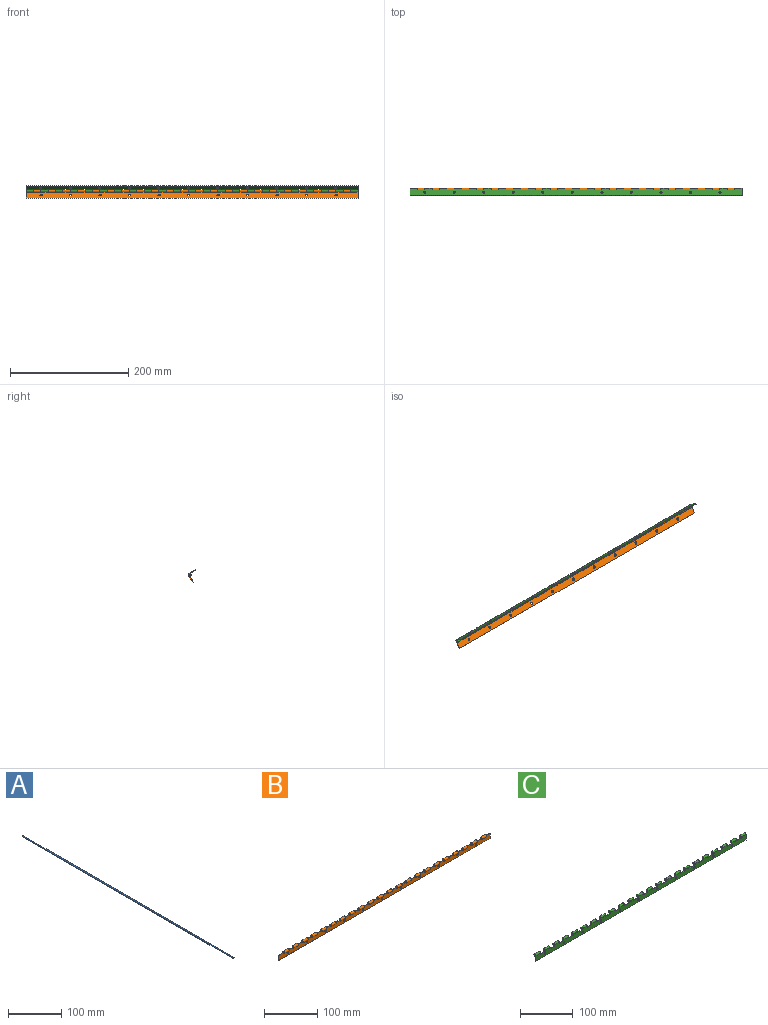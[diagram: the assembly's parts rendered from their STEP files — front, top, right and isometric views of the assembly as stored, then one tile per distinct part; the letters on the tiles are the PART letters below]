
ASSEMBLY  parts=3 mates=1
PART A: 3 faces, bbox 2.8x562.5x2.8 mm
  f0: cylinder r=1.4mm len=562.5mm, axis (0,1,0), area 4948mm2, adj f1,f2
  f1: plane 2.8x2.8mm, normal (0,-1,0), area 6.2mm2, adj f0
  f2: plane 2.8x2.8mm, normal (0,1,0), area 6.2mm2, adj f0
PART B: 193 faces, bbox 562.5x5x16 mm
  f0: plane 562.5x13.5mm, normal (0,-1,0), area 6880.5mm2, adj f4,f5,f8,f11,f14,f17,f20,f23
  f1: plane 562.5x13.5mm, normal (0,1,0), area 6880.5mm2, adj f3,f5,f7,f10,f13,f16,f19,f22
  f2: plane 12.5x0.87mm, normal (0,0.87,0.5), area 12.5mm2, adj f3,f4,f179,f182
  f3: cylinder r=2.5mm len=12.5mm, axis (-1,0,0), area 163.6mm2, adj f1,f2,f179,f182
  f4: cylinder r=1.5mm len=12.5mm, axis (-1,0,0), area 98.2mm2, adj f0,f2,f179,f182
  f5: plane 11.5x1mm, normal (1,0,0), area 11.5mm2, adj f0,f1,f70,f181
  f6: plane 12.5x0.87mm, normal (0,0.87,0.5), area 12.5mm2, adj f7,f8,f174,f178
  f7: cylinder r=2.5mm len=12.5mm, axis (-1,0,0), area 163.6mm2, adj f1,f6,f174,f178
  f8: cylinder r=1.5mm len=12.5mm, axis (-1,0,0), area 98.2mm2, adj f0,f6,f174,f178
  f9: plane 12.5x0.87mm, normal (0,0.87,0.5), area 12.5mm2, adj f10,f11,f169,f173
  f10: cylinder r=2.5mm len=12.5mm, axis (-1,0,0), area 163.6mm2, adj f1,f9,f169,f173
  f11: cylinder r=1.5mm len=12.5mm, axis (-1,0,0), area 98.2mm2, adj f0,f9,f169,f173
  f12: plane 12.5x0.87mm, normal (0,0.87,0.5), area 12.5mm2, adj f13,f14,f164,f168
  f13: cylinder r=2.5mm len=12.5mm, axis (-1,0,0), area 163.6mm2, adj f1,f12,f164,f168
  f14: cylinder r=1.5mm len=12.5mm, axis (-1,0,0), area 98.2mm2, adj f0,f12,f164,f168
  f15: plane 12.5x0.87mm, normal (0,0.87,0.5), area 12.5mm2, adj f16,f17,f159,f163
  f16: cylinder r=2.5mm len=12.5mm, axis (-1,0,0), area 163.6mm2, adj f1,f15,f159,f163
  f17: cylinder r=1.5mm len=12.5mm, axis (-1,0,0), area 98.2mm2, adj f0,f15,f159,f163
  f18: plane 12.5x0.87mm, normal (0,0.87,0.5), area 12.5mm2, adj f19,f20,f154,f158
  f19: cylinder r=2.5mm len=12.5mm, axis (-1,0,0), area 163.6mm2, adj f1,f18,f154,f158
  f20: cylinder r=1.5mm len=12.5mm, axis (-1,0,0), area 98.2mm2, adj f0,f18,f154,f158
  f21: plane 12.5x0.87mm, normal (0,0.87,0.5), area 12.5mm2, adj f22,f23,f149,f153
  f22: cylinder r=2.5mm len=12.5mm, axis (-1,0,0), area 163.6mm2, adj f1,f21,f149,f153
  f23: cylinder r=1.5mm len=12.5mm, axis (-1,0,0), area 98.2mm2, adj f0,f21,f149,f153
  f24: plane 12.5x0.87mm, normal (0,0.87,0.5), area 12.5mm2, adj f25,f26,f144,f148
  f25: cylinder r=2.5mm len=12.5mm, axis (-1,0,0), area 163.6mm2, adj f1,f24,f144,f148
  f26: cylinder r=1.5mm len=12.5mm, axis (-1,0,0), area 98.2mm2, adj f0,f24,f144,f148
  f27: plane 12.5x0.87mm, normal (0,0.87,0.5), area 12.5mm2, adj f28,f29,f139,f143
  f28: cylinder r=2.5mm len=12.5mm, axis (-1,0,0), area 163.6mm2, adj f1,f27,f139,f143
  f29: cylinder r=1.5mm len=12.5mm, axis (-1,0,0), area 98.2mm2, adj f0,f27,f139,f143
  f30: plane 12.5x0.87mm, normal (0,0.87,0.5), area 12.5mm2, adj f31,f32,f134,f138
  f31: cylinder r=2.5mm len=12.5mm, axis (-1,0,0), area 163.6mm2, adj f1,f30,f134,f138
  f32: cylinder r=1.5mm len=12.5mm, axis (-1,0,0), area 98.2mm2, adj f0,f30,f134,f138
  f33: plane 12.5x0.87mm, normal (0,0.87,0.5), area 12.5mm2, adj f34,f35,f129,f133
  f34: cylinder r=2.5mm len=12.5mm, axis (-1,0,0), area 163.6mm2, adj f1,f33,f129,f133
  f35: cylinder r=1.5mm len=12.5mm, axis (-1,0,0), area 98.2mm2, adj f0,f33,f129,f133
  f36: plane 12.5x0.87mm, normal (0,0.87,0.5), area 12.5mm2, adj f37,f38,f124,f128
  f37: cylinder r=2.5mm len=12.5mm, axis (-1,0,0), area 163.6mm2, adj f1,f36,f124,f128
  f38: cylinder r=1.5mm len=12.5mm, axis (-1,0,0), area 98.2mm2, adj f0,f36,f124,f128
  f39: plane 12.5x0.87mm, normal (0,0.87,0.5), area 12.5mm2, adj f40,f41,f119,f123
  f40: cylinder r=2.5mm len=12.5mm, axis (-1,0,0), area 163.6mm2, adj f1,f39,f119,f123
  f41: cylinder r=1.5mm len=12.5mm, axis (-1,0,0), area 98.2mm2, adj f0,f39,f119,f123
  f42: plane 12.5x0.87mm, normal (0,0.87,0.5), area 12.5mm2, adj f43,f44,f114,f118
  f43: cylinder r=2.5mm len=12.5mm, axis (-1,0,0), area 163.6mm2, adj f1,f42,f114,f118
  f44: cylinder r=1.5mm len=12.5mm, axis (-1,0,0), area 98.2mm2, adj f0,f42,f114,f118
  f45: plane 12.5x0.87mm, normal (0,0.87,0.5), area 12.5mm2, adj f46,f47,f109,f113
  f46: cylinder r=2.5mm len=12.5mm, axis (-1,0,0), area 163.6mm2, adj f1,f45,f109,f113
  f47: cylinder r=1.5mm len=12.5mm, axis (-1,0,0), area 98.2mm2, adj f0,f45,f109,f113
  f48: plane 12.5x0.87mm, normal (0,0.87,0.5), area 12.5mm2, adj f49,f50,f104,f108
  f49: cylinder r=2.5mm len=12.5mm, axis (-1,0,0), area 163.6mm2, adj f1,f48,f104,f108
  f50: cylinder r=1.5mm len=12.5mm, axis (-1,0,0), area 98.2mm2, adj f0,f48,f104,f108
  f51: plane 12.5x0.87mm, normal (0,0.87,0.5), area 12.5mm2, adj f52,f53,f99,f103
  f52: cylinder r=2.5mm len=12.5mm, axis (-1,0,0), area 163.6mm2, adj f1,f51,f99,f103
  f53: cylinder r=1.5mm len=12.5mm, axis (-1,0,0), area 98.2mm2, adj f0,f51,f99,f103
  f54: plane 12.5x0.87mm, normal (0,0.87,0.5), area 12.5mm2, adj f55,f56,f94,f98
  f55: cylinder r=2.5mm len=12.5mm, axis (-1,0,0), area 163.6mm2, adj f1,f54,f94,f98
  f56: cylinder r=1.5mm len=12.5mm, axis (-1,0,0), area 98.2mm2, adj f0,f54,f94,f98
  f57: plane 12.5x0.87mm, normal (0,0.87,0.5), area 12.5mm2, adj f58,f59,f89,f93
  f58: cylinder r=2.5mm len=12.5mm, axis (-1,0,0), area 163.6mm2, adj f1,f57,f89,f93
  f59: cylinder r=1.5mm len=12.5mm, axis (-1,0,0), area 98.2mm2, adj f0,f57,f89,f93
  f60: plane 12.5x0.87mm, normal (0,0.87,0.5), area 12.5mm2, adj f61,f62,f84,f88
  f61: cylinder r=2.5mm len=12.5mm, axis (-1,0,0), area 163.6mm2, adj f1,f60,f84,f88
  f62: cylinder r=1.5mm len=12.5mm, axis (-1,0,0), area 98.2mm2, adj f0,f60,f84,f88
  f63: plane 12.5x0.87mm, normal (0,0.87,0.5), area 12.5mm2, adj f64,f65,f78,f83
  f64: cylinder r=2.5mm len=12.5mm, axis (-1,0,0), area 163.6mm2, adj f1,f63,f78,f83
  f65: cylinder r=1.5mm len=12.5mm, axis (-1,0,0), area 98.2mm2, adj f0,f63,f78,f83
  f66: plane 12.5x0.87mm, normal (0,0.87,0.5), area 12.5mm2, adj f67,f68,f73,f77
  f67: cylinder r=2.5mm len=12.5mm, axis (-1,0,0), area 163.6mm2, adj f1,f66,f73,f77
  f68: cylinder r=1.5mm len=12.5mm, axis (-1,0,0), area 98.2mm2, adj f0,f66,f73,f77
  f69: plane 11.5x1mm, normal (-1,0,0), area 11.5mm2, adj f0,f1,f70,f71
  f70: plane 562.5x1mm, normal (0,0,-1), area 562.5mm2, adj f0,f1,f5,f69
  f71: plane 12.5x1mm, normal (0,0,1), area 12.5mm2, adj f0,f1,f69,f72
  f72: plane 2x1mm, normal (-1,0,0), area 2mm2, adj f0,f1,f71,f73
  f73: plane 5x5mm, normal (-1,0,0), area 10.5mm2, adj f66,f67,f68,f72
  f74: plane 12.5x1mm, normal (0,0,1), area 12.5mm2, adj f0,f1,f75,f76
  f75: plane 2x1mm, normal (1,0,0), area 2mm2, adj f0,f1,f74,f77
  f76: plane 2x1mm, normal (-1,0,0), area 2mm2, adj f0,f1,f74,f78
  f77: plane 5x5mm, normal (1,0,0), area 10.5mm2, adj f66,f67,f68,f75
  f78: plane 5x5mm, normal (-1,0,0), area 10.5mm2, adj f63,f64,f65,f76
  f79: cylinder r=2mm len=4mm, axis (0,1,0), area 12.6mm2, adj f0,f1
  f80: plane 12.5x1mm, normal (0,0,1), area 12.5mm2, adj f0,f1,f81,f82
  f81: plane 2x1mm, normal (1,0,0), area 2mm2, adj f0,f1,f80,f83
  f82: plane 2x1mm, normal (-1,0,0), area 2mm2, adj f0,f1,f80,f84
  f83: plane 5x5mm, normal (1,0,0), area 10.5mm2, adj f63,f64,f65,f81
  f84: plane 5x5mm, normal (-1,0,0), area 10.5mm2, adj f60,f61,f62,f82
  f85: plane 12.5x1mm, normal (0,0,1), area 12.5mm2, adj f0,f1,f86,f87
  f86: plane 2x1mm, normal (1,0,0), area 2mm2, adj f0,f1,f85,f88
  f87: plane 2x1mm, normal (-1,0,0), area 2mm2, adj f0,f1,f85,f89
  f88: plane 5x5mm, normal (1,0,0), area 10.5mm2, adj f60,f61,f62,f86
  f89: plane 5x5mm, normal (-1,0,0), area 10.5mm2, adj f57,f58,f59,f87
  f90: plane 12.5x1mm, normal (0,0,1), area 12.5mm2, adj f0,f1,f91,f92
  f91: plane 2x1mm, normal (1,0,0), area 2mm2, adj f0,f1,f90,f93
  f92: plane 2x1mm, normal (-1,0,0), area 2mm2, adj f0,f1,f90,f94
  f93: plane 5x5mm, normal (1,0,0), area 10.5mm2, adj f57,f58,f59,f91
  f94: plane 5x5mm, normal (-1,0,0), area 10.5mm2, adj f54,f55,f56,f92
  f95: plane 12.5x1mm, normal (0,0,1), area 12.5mm2, adj f0,f1,f96,f97
  f96: plane 2x1mm, normal (1,0,0), area 2mm2, adj f0,f1,f95,f98
  f97: plane 2x1mm, normal (-1,0,0), area 2mm2, adj f0,f1,f95,f99
  f98: plane 5x5mm, normal (1,0,0), area 10.5mm2, adj f54,f55,f56,f96
  f99: plane 5x5mm, normal (-1,0,0), area 10.5mm2, adj f51,f52,f53,f97
  f100: plane 12.5x1mm, normal (0,0,1), area 12.5mm2, adj f0,f1,f101,f102
  f101: plane 2x1mm, normal (1,0,0), area 2mm2, adj f0,f1,f100,f103
  f102: plane 2x1mm, normal (-1,0,0), area 2mm2, adj f0,f1,f100,f104
  f103: plane 5x5mm, normal (1,0,0), area 10.5mm2, adj f51,f52,f53,f101
  f104: plane 5x5mm, normal (-1,0,0), area 10.5mm2, adj f48,f49,f50,f102
  f105: plane 12.5x1mm, normal (0,0,1), area 12.5mm2, adj f0,f1,f106,f107
  f106: plane 2x1mm, normal (1,0,0), area 2mm2, adj f0,f1,f105,f108
  f107: plane 2x1mm, normal (-1,0,0), area 2mm2, adj f0,f1,f105,f109
  f108: plane 5x5mm, normal (1,0,0), area 10.5mm2, adj f48,f49,f50,f106
  f109: plane 5x5mm, normal (-1,0,0), area 10.5mm2, adj f45,f46,f47,f107
  f110: plane 12.5x1mm, normal (0,0,1), area 12.5mm2, adj f0,f1,f111,f112
  f111: plane 2x1mm, normal (1,0,0), area 2mm2, adj f0,f1,f110,f113
  f112: plane 2x1mm, normal (-1,0,0), area 2mm2, adj f0,f1,f110,f114
  f113: plane 5x5mm, normal (1,0,0), area 10.5mm2, adj f45,f46,f47,f111
  f114: plane 5x5mm, normal (-1,0,0), area 10.5mm2, adj f42,f43,f44,f112
  f115: plane 12.5x1mm, normal (0,0,1), area 12.5mm2, adj f0,f1,f116,f117
  f116: plane 2x1mm, normal (1,0,0), area 2mm2, adj f0,f1,f115,f118
  f117: plane 2x1mm, normal (-1,0,0), area 2mm2, adj f0,f1,f115,f119
  f118: plane 5x5mm, normal (1,0,0), area 10.5mm2, adj f42,f43,f44,f116
  f119: plane 5x5mm, normal (-1,0,0), area 10.5mm2, adj f39,f40,f41,f117
  f120: plane 12.5x1mm, normal (0,0,1), area 12.5mm2, adj f0,f1,f121,f122
  f121: plane 2x1mm, normal (1,0,0), area 2mm2, adj f0,f1,f120,f123
  f122: plane 2x1mm, normal (-1,0,0), area 2mm2, adj f0,f1,f120,f124
  f123: plane 5x5mm, normal (1,0,0), area 10.5mm2, adj f39,f40,f41,f121
  f124: plane 5x5mm, normal (-1,0,0), area 10.5mm2, adj f36,f37,f38,f122
  f125: plane 12.5x1mm, normal (0,0,1), area 12.5mm2, adj f0,f1,f126,f127
  f126: plane 2x1mm, normal (1,0,0), area 2mm2, adj f0,f1,f125,f128
  f127: plane 2x1mm, normal (-1,0,0), area 2mm2, adj f0,f1,f125,f129
  f128: plane 5x5mm, normal (1,0,0), area 10.5mm2, adj f36,f37,f38,f126
  f129: plane 5x5mm, normal (-1,0,0), area 10.5mm2, adj f33,f34,f35,f127
  f130: plane 12.5x1mm, normal (0,0,1), area 12.5mm2, adj f0,f1,f131,f132
  f131: plane 2x1mm, normal (1,0,0), area 2mm2, adj f0,f1,f130,f133
  f132: plane 2x1mm, normal (-1,0,0), area 2mm2, adj f0,f1,f130,f134
  f133: plane 5x5mm, normal (1,0,0), area 10.5mm2, adj f33,f34,f35,f131
  f134: plane 5x5mm, normal (-1,0,0), area 10.5mm2, adj f30,f31,f32,f132
  f135: plane 12.5x1mm, normal (0,0,1), area 12.5mm2, adj f0,f1,f136,f137
  f136: plane 2x1mm, normal (1,0,0), area 2mm2, adj f0,f1,f135,f138
  f137: plane 2x1mm, normal (-1,0,0), area 2mm2, adj f0,f1,f135,f139
  f138: plane 5x5mm, normal (1,0,0), area 10.5mm2, adj f30,f31,f32,f136
  f139: plane 5x5mm, normal (-1,0,0), area 10.5mm2, adj f27,f28,f29,f137
  f140: plane 12.5x1mm, normal (0,0,1), area 12.5mm2, adj f0,f1,f141,f142
  f141: plane 2x1mm, normal (1,0,0), area 2mm2, adj f0,f1,f140,f143
  f142: plane 2x1mm, normal (-1,0,0), area 2mm2, adj f0,f1,f140,f144
  f143: plane 5x5mm, normal (1,0,0), area 10.5mm2, adj f27,f28,f29,f141
  f144: plane 5x5mm, normal (-1,0,0), area 10.5mm2, adj f24,f25,f26,f142
  f145: plane 12.5x1mm, normal (0,0,1), area 12.5mm2, adj f0,f1,f146,f147
  f146: plane 2x1mm, normal (1,0,0), area 2mm2, adj f0,f1,f145,f148
  f147: plane 2x1mm, normal (-1,0,0), area 2mm2, adj f0,f1,f145,f149
  f148: plane 5x5mm, normal (1,0,0), area 10.5mm2, adj f24,f25,f26,f146
  f149: plane 5x5mm, normal (-1,0,0), area 10.5mm2, adj f21,f22,f23,f147
  f150: plane 12.5x1mm, normal (0,0,1), area 12.5mm2, adj f0,f1,f151,f152
  f151: plane 2x1mm, normal (1,0,0), area 2mm2, adj f0,f1,f150,f153
  f152: plane 2x1mm, normal (-1,0,0), area 2mm2, adj f0,f1,f150,f154
  f153: plane 5x5mm, normal (1,0,0), area 10.5mm2, adj f21,f22,f23,f151
  f154: plane 5x5mm, normal (-1,0,0), area 10.5mm2, adj f18,f19,f20,f152
  f155: plane 12.5x1mm, normal (0,0,1), area 12.5mm2, adj f0,f1,f156,f157
  f156: plane 2x1mm, normal (1,0,0), area 2mm2, adj f0,f1,f155,f158
  f157: plane 2x1mm, normal (-1,0,0), area 2mm2, adj f0,f1,f155,f159
  f158: plane 5x5mm, normal (1,0,0), area 10.5mm2, adj f18,f19,f20,f156
  f159: plane 5x5mm, normal (-1,0,0), area 10.5mm2, adj f15,f16,f17,f157
  f160: plane 12.5x1mm, normal (0,0,1), area 12.5mm2, adj f0,f1,f161,f162
  f161: plane 2x1mm, normal (1,0,0), area 2mm2, adj f0,f1,f160,f163
  f162: plane 2x1mm, normal (-1,0,0), area 2mm2, adj f0,f1,f160,f164
  f163: plane 5x5mm, normal (1,0,0), area 10.5mm2, adj f15,f16,f17,f161
  f164: plane 5x5mm, normal (-1,0,0), area 10.5mm2, adj f12,f13,f14,f162
  f165: plane 12.5x1mm, normal (0,0,1), area 12.5mm2, adj f0,f1,f166,f167
  f166: plane 2x1mm, normal (1,0,0), area 2mm2, adj f0,f1,f165,f168
  f167: plane 2x1mm, normal (-1,0,0), area 2mm2, adj f0,f1,f165,f169
  f168: plane 5x5mm, normal (1,0,0), area 10.5mm2, adj f12,f13,f14,f166
  f169: plane 5x5mm, normal (-1,0,0), area 10.5mm2, adj f9,f10,f11,f167
  f170: plane 12.5x1mm, normal (0,0,1), area 12.5mm2, adj f0,f1,f171,f172
  f171: plane 2x1mm, normal (1,0,0), area 2mm2, adj f0,f1,f170,f173
  f172: plane 2x1mm, normal (-1,0,0), area 2mm2, adj f0,f1,f170,f174
  f173: plane 5x5mm, normal (1,0,0), area 10.5mm2, adj f9,f10,f11,f171
  f174: plane 5x5mm, normal (-1,0,0), area 10.5mm2, adj f6,f7,f8,f172
  f175: plane 12.5x1mm, normal (0,0,1), area 12.5mm2, adj f0,f1,f176,f177
  f176: plane 2x1mm, normal (1,0,0), area 2mm2, adj f0,f1,f175,f178
  f177: plane 2x1mm, normal (-1,0,0), area 2mm2, adj f0,f1,f175,f179
  f178: plane 5x5mm, normal (1,0,0), area 10.5mm2, adj f6,f7,f8,f176
  f179: plane 5x5mm, normal (-1,0,0), area 10.5mm2, adj f2,f3,f4,f177
  f180: plane 2x1mm, normal (1,0,0), area 2mm2, adj f0,f1,f181,f182
  f181: plane 12.5x1mm, normal (0,0,1), area 12.5mm2, adj f0,f1,f5,f180
  f182: plane 5x5mm, normal (1,0,0), area 10.5mm2, adj f2,f3,f4,f180
  f183: cylinder r=2mm len=4mm, axis (0,1,0), area 12.6mm2, adj f0,f1
  f184: cylinder r=2mm len=4mm, axis (0,1,0), area 12.6mm2, adj f0,f1
  f185: cylinder r=2mm len=4mm, axis (0,1,0), area 12.6mm2, adj f0,f1
  f186: cylinder r=2mm len=4mm, axis (0,1,0), area 12.6mm2, adj f0,f1
  f187: cylinder r=2mm len=4mm, axis (0,1,0), area 12.6mm2, adj f0,f1
  f188: cylinder r=2mm len=4mm, axis (0,1,0), area 12.6mm2, adj f0,f1
  f189: cylinder r=2mm len=4mm, axis (0,1,0), area 12.6mm2, adj f0,f1
  f190: cylinder r=2mm len=4mm, axis (0,1,0), area 12.6mm2, adj f0,f1
  f191: cylinder r=2mm len=4mm, axis (0,1,0), area 12.6mm2, adj f0,f1
  f192: cylinder r=2mm len=4mm, axis (0,1,0), area 12.6mm2, adj f0,f1
PART C: 153 faces, bbox 562.5x5x15.5 mm
  f0: plane 12.5x0.87mm, normal (0,-0.87,0.5), area 12.5mm2, adj f1,f2,f137,f139
  f1: cylinder r=2.5mm len=12.5mm, axis (1,0,0), area 163.6mm2, adj f0,f69,f137,f139
  f2: cylinder r=1.5mm len=12.5mm, axis (1,0,0), area 98.2mm2, adj f0,f70,f137,f139
  f3: plane 12.5x0.87mm, normal (0,-0.87,0.5), area 12.5mm2, adj f4,f5,f134,f136
  f4: cylinder r=2.5mm len=12.5mm, axis (1,0,0), area 163.6mm2, adj f3,f69,f134,f136
  f5: cylinder r=1.5mm len=12.5mm, axis (1,0,0), area 98.2mm2, adj f3,f70,f134,f136
  f6: plane 12.5x0.87mm, normal (0,-0.87,0.5), area 12.5mm2, adj f7,f8,f131,f133
  f7: cylinder r=2.5mm len=12.5mm, axis (1,0,0), area 163.6mm2, adj f6,f69,f131,f133
  f8: cylinder r=1.5mm len=12.5mm, axis (1,0,0), area 98.2mm2, adj f6,f70,f131,f133
  f9: plane 12.5x0.87mm, normal (0,-0.87,0.5), area 12.5mm2, adj f10,f11,f128,f130
  f10: cylinder r=2.5mm len=12.5mm, axis (1,0,0), area 163.6mm2, adj f9,f69,f128,f130
  f11: cylinder r=1.5mm len=12.5mm, axis (1,0,0), area 98.2mm2, adj f9,f70,f128,f130
  f12: plane 12.5x0.87mm, normal (0,-0.87,0.5), area 12.5mm2, adj f13,f14,f125,f127
  f13: cylinder r=2.5mm len=12.5mm, axis (1,0,0), area 163.6mm2, adj f12,f69,f125,f127
  f14: cylinder r=1.5mm len=12.5mm, axis (1,0,0), area 98.2mm2, adj f12,f70,f125,f127
  f15: plane 12.5x0.87mm, normal (0,-0.87,0.5), area 12.5mm2, adj f16,f17,f122,f124
  f16: cylinder r=2.5mm len=12.5mm, axis (1,0,0), area 163.6mm2, adj f15,f69,f122,f124
  f17: cylinder r=1.5mm len=12.5mm, axis (1,0,0), area 98.2mm2, adj f15,f70,f122,f124
  f18: plane 12.5x0.87mm, normal (0,-0.87,0.5), area 12.5mm2, adj f19,f20,f119,f121
  f19: cylinder r=2.5mm len=12.5mm, axis (1,0,0), area 163.6mm2, adj f18,f69,f119,f121
  f20: cylinder r=1.5mm len=12.5mm, axis (1,0,0), area 98.2mm2, adj f18,f70,f119,f121
  f21: plane 12.5x0.87mm, normal (0,-0.87,0.5), area 12.5mm2, adj f22,f23,f116,f118
  f22: cylinder r=2.5mm len=12.5mm, axis (1,0,0), area 163.6mm2, adj f21,f69,f116,f118
  f23: cylinder r=1.5mm len=12.5mm, axis (1,0,0), area 98.2mm2, adj f21,f70,f116,f118
  f24: plane 12.5x0.87mm, normal (0,-0.87,0.5), area 12.5mm2, adj f25,f26,f113,f115
  f25: cylinder r=2.5mm len=12.5mm, axis (1,0,0), area 163.6mm2, adj f24,f69,f113,f115
  f26: cylinder r=1.5mm len=12.5mm, axis (1,0,0), area 98.2mm2, adj f24,f70,f113,f115
  f27: plane 12.5x0.87mm, normal (0,-0.87,0.5), area 12.5mm2, adj f28,f29,f110,f112
  f28: cylinder r=2.5mm len=12.5mm, axis (1,0,0), area 163.6mm2, adj f27,f69,f110,f112
  f29: cylinder r=1.5mm len=12.5mm, axis (1,0,0), area 98.2mm2, adj f27,f70,f110,f112
  f30: plane 12.5x0.87mm, normal (0,-0.87,0.5), area 12.5mm2, adj f31,f32,f107,f109
  f31: cylinder r=2.5mm len=12.5mm, axis (1,0,0), area 163.6mm2, adj f30,f69,f107,f109
  f32: cylinder r=1.5mm len=12.5mm, axis (1,0,0), area 98.2mm2, adj f30,f70,f107,f109
  f33: plane 12.5x0.87mm, normal (0,-0.87,0.5), area 12.5mm2, adj f34,f35,f104,f106
  f34: cylinder r=2.5mm len=12.5mm, axis (1,0,0), area 163.6mm2, adj f33,f69,f104,f106
  f35: cylinder r=1.5mm len=12.5mm, axis (1,0,0), area 98.2mm2, adj f33,f70,f104,f106
  f36: plane 12.5x0.87mm, normal (0,-0.87,0.5), area 12.5mm2, adj f37,f38,f101,f103
  f37: cylinder r=2.5mm len=12.5mm, axis (1,0,0), area 163.6mm2, adj f36,f69,f101,f103
  f38: cylinder r=1.5mm len=12.5mm, axis (1,0,0), area 98.2mm2, adj f36,f70,f101,f103
  f39: plane 12.5x0.87mm, normal (0,-0.87,0.5), area 12.5mm2, adj f40,f41,f98,f100
  f40: cylinder r=2.5mm len=12.5mm, axis (1,0,0), area 163.6mm2, adj f39,f69,f98,f100
  f41: cylinder r=1.5mm len=12.5mm, axis (1,0,0), area 98.2mm2, adj f39,f70,f98,f100
  f42: plane 12.5x0.87mm, normal (0,-0.87,0.5), area 12.5mm2, adj f43,f44,f95,f97
  f43: cylinder r=2.5mm len=12.5mm, axis (1,0,0), area 163.6mm2, adj f42,f69,f95,f97
  f44: cylinder r=1.5mm len=12.5mm, axis (1,0,0), area 98.2mm2, adj f42,f70,f95,f97
  f45: plane 12.5x0.87mm, normal (0,-0.87,0.5), area 12.5mm2, adj f46,f47,f92,f94
  f46: cylinder r=2.5mm len=12.5mm, axis (1,0,0), area 163.6mm2, adj f45,f69,f92,f94
  f47: cylinder r=1.5mm len=12.5mm, axis (1,0,0), area 98.2mm2, adj f45,f70,f92,f94
  f48: plane 12.5x0.87mm, normal (0,-0.87,0.5), area 12.5mm2, adj f49,f50,f89,f91
  f49: cylinder r=2.5mm len=12.5mm, axis (1,0,0), area 163.6mm2, adj f48,f69,f89,f91
  f50: cylinder r=1.5mm len=12.5mm, axis (1,0,0), area 98.2mm2, adj f48,f70,f89,f91
  f51: plane 12.5x0.87mm, normal (0,-0.87,0.5), area 12.5mm2, adj f52,f53,f86,f88
  f52: cylinder r=2.5mm len=12.5mm, axis (1,0,0), area 163.6mm2, adj f51,f69,f86,f88
  f53: cylinder r=1.5mm len=12.5mm, axis (1,0,0), area 98.2mm2, adj f51,f70,f86,f88
  f54: plane 12.5x0.87mm, normal (0,-0.87,0.5), area 12.5mm2, adj f55,f56,f83,f85
  f55: cylinder r=2.5mm len=12.5mm, axis (1,0,0), area 163.6mm2, adj f54,f69,f83,f85
  f56: cylinder r=1.5mm len=12.5mm, axis (1,0,0), area 98.2mm2, adj f54,f70,f83,f85
  f57: plane 12.5x0.87mm, normal (0,-0.87,0.5), area 12.5mm2, adj f58,f59,f80,f82
  f58: cylinder r=2.5mm len=12.5mm, axis (1,0,0), area 163.6mm2, adj f57,f69,f80,f82
  f59: cylinder r=1.5mm len=12.5mm, axis (1,0,0), area 98.2mm2, adj f57,f70,f80,f82
  f60: plane 12.5x0.87mm, normal (0,-0.87,0.5), area 12.5mm2, adj f61,f62,f77,f79
  f61: cylinder r=2.5mm len=12.5mm, axis (1,0,0), area 163.6mm2, adj f60,f69,f77,f79
  f62: cylinder r=1.5mm len=12.5mm, axis (1,0,0), area 98.2mm2, adj f60,f70,f77,f79
  f63: plane 12.5x0.87mm, normal (0,-0.87,0.5), area 12.5mm2, adj f64,f65,f72,f76
  f64: cylinder r=2.5mm len=12.5mm, axis (1,0,0), area 163.6mm2, adj f63,f69,f72,f76
  f65: cylinder r=1.5mm len=12.5mm, axis (1,0,0), area 98.2mm2, adj f63,f70,f72,f76
  f66: plane 13x1mm, normal (-1,0,0), area 13mm2, adj f67,f69,f70,f72
  f67: plane 562.5x1mm, normal (0,0,-1), area 562.5mm2, adj f66,f68,f69,f70
  f68: plane 13x1mm, normal (1,0,0), area 13mm2, adj f67,f69,f70,f73
  f69: plane 562.5x13mm, normal (0,-1,0), area 6486.8mm2, adj f1,f4,f7,f10,f13,f16,f19,f22
  f70: plane 562.5x13mm, normal (0,1,0), area 6486.8mm2, adj f2,f5,f8,f11,f14,f17,f20,f23
  f71: plane 12.5x0.87mm, normal (0,-0.87,0.5), area 12.5mm2, adj f73,f74,f75,f140
  f72: plane 5x5mm, normal (-1,0,0), area 10.5mm2, adj f63,f64,f65,f66
  f73: plane 5x5mm, normal (1,0,0), area 10.5mm2, adj f68,f71,f74,f75
  f74: cylinder r=2.5mm len=12.5mm, axis (1,0,0), area 163.6mm2, adj f69,f71,f73,f140
  f75: cylinder r=1.5mm len=12.5mm, axis (1,0,0), area 98.2mm2, adj f70,f71,f73,f140
  f76: plane 5x5mm, normal (1,0,0), area 13mm2, adj f63,f64,f65,f69,f70,f78
  f77: plane 5x5mm, normal (-1,0,0), area 13mm2, adj f60,f61,f62,f69,f70,f78
  f78: plane 12.5x1mm, normal (0,0,1), area 12.5mm2, adj f69,f70,f76,f77
  f79: plane 5x5mm, normal (1,0,0), area 13mm2, adj f60,f61,f62,f69,f70,f81
  f80: plane 5x5mm, normal (-1,0,0), area 13mm2, adj f57,f58,f59,f69,f70,f81
  f81: plane 12.5x1mm, normal (0,0,1), area 12.5mm2, adj f69,f70,f79,f80
  f82: plane 5x5mm, normal (1,0,0), area 13mm2, adj f57,f58,f59,f69,f70,f84
  f83: plane 5x5mm, normal (-1,0,0), area 13mm2, adj f54,f55,f56,f69,f70,f84
  f84: plane 12.5x1mm, normal (0,0,1), area 12.5mm2, adj f69,f70,f82,f83
  f85: plane 5x5mm, normal (1,0,0), area 13mm2, adj f54,f55,f56,f69,f70,f87
  f86: plane 5x5mm, normal (-1,0,0), area 13mm2, adj f51,f52,f53,f69,f70,f87
  f87: plane 12.5x1mm, normal (0,0,1), area 12.5mm2, adj f69,f70,f85,f86
  f88: plane 5x5mm, normal (1,0,0), area 13mm2, adj f51,f52,f53,f69,f70,f90
  f89: plane 5x5mm, normal (-1,0,0), area 13mm2, adj f48,f49,f50,f69,f70,f90
  f90: plane 12.5x1mm, normal (0,0,1), area 12.5mm2, adj f69,f70,f88,f89
  f91: plane 5x5mm, normal (1,0,0), area 13mm2, adj f48,f49,f50,f69,f70,f93
  f92: plane 5x5mm, normal (-1,0,0), area 13mm2, adj f45,f46,f47,f69,f70,f93
  f93: plane 12.5x1mm, normal (0,0,1), area 12.5mm2, adj f69,f70,f91,f92
  f94: plane 5x5mm, normal (1,0,0), area 13mm2, adj f45,f46,f47,f69,f70,f96
  f95: plane 5x5mm, normal (-1,0,0), area 13mm2, adj f42,f43,f44,f69,f70,f96
  f96: plane 12.5x1mm, normal (0,0,1), area 12.5mm2, adj f69,f70,f94,f95
  f97: plane 5x5mm, normal (1,0,0), area 13mm2, adj f42,f43,f44,f69,f70,f99
  f98: plane 5x5mm, normal (-1,0,0), area 13mm2, adj f39,f40,f41,f69,f70,f99
  f99: plane 12.5x1mm, normal (0,0,1), area 12.5mm2, adj f69,f70,f97,f98
  f100: plane 5x5mm, normal (1,0,0), area 13mm2, adj f39,f40,f41,f69,f70,f102
  f101: plane 5x5mm, normal (-1,0,0), area 13mm2, adj f36,f37,f38,f69,f70,f102
  f102: plane 12.5x1mm, normal (0,0,1), area 12.5mm2, adj f69,f70,f100,f101
  f103: plane 5x5mm, normal (1,0,0), area 13mm2, adj f36,f37,f38,f69,f70,f105
  f104: plane 5x5mm, normal (-1,0,0), area 13mm2, adj f33,f34,f35,f69,f70,f105
  f105: plane 12.5x1mm, normal (0,0,1), area 12.5mm2, adj f69,f70,f103,f104
  f106: plane 5x5mm, normal (1,0,0), area 13mm2, adj f33,f34,f35,f69,f70,f108
  f107: plane 5x5mm, normal (-1,0,0), area 13mm2, adj f30,f31,f32,f69,f70,f108
  f108: plane 12.5x1mm, normal (0,0,1), area 12.5mm2, adj f69,f70,f106,f107
  f109: plane 5x5mm, normal (1,0,0), area 13mm2, adj f30,f31,f32,f69,f70,f111
  f110: plane 5x5mm, normal (-1,0,0), area 13mm2, adj f27,f28,f29,f69,f70,f111
  f111: plane 12.5x1mm, normal (0,0,1), area 12.5mm2, adj f69,f70,f109,f110
  f112: plane 5x5mm, normal (1,0,0), area 13mm2, adj f27,f28,f29,f69,f70,f114
  f113: plane 5x5mm, normal (-1,0,0), area 13mm2, adj f24,f25,f26,f69,f70,f114
  f114: plane 12.5x1mm, normal (0,0,1), area 12.5mm2, adj f69,f70,f112,f113
  f115: plane 5x5mm, normal (1,0,0), area 13mm2, adj f24,f25,f26,f69,f70,f117
  f116: plane 5x5mm, normal (-1,0,0), area 13mm2, adj f21,f22,f23,f69,f70,f117
  f117: plane 12.5x1mm, normal (0,0,1), area 12.5mm2, adj f69,f70,f115,f116
  f118: plane 5x5mm, normal (1,0,0), area 13mm2, adj f21,f22,f23,f69,f70,f120
  f119: plane 5x5mm, normal (-1,0,0), area 13mm2, adj f18,f19,f20,f69,f70,f120
  f120: plane 12.5x1mm, normal (0,0,1), area 12.5mm2, adj f69,f70,f118,f119
  f121: plane 5x5mm, normal (1,0,0), area 13mm2, adj f18,f19,f20,f69,f70,f123
  f122: plane 5x5mm, normal (-1,0,0), area 13mm2, adj f15,f16,f17,f69,f70,f123
  f123: plane 12.5x1mm, normal (0,0,1), area 12.5mm2, adj f69,f70,f121,f122
  f124: plane 5x5mm, normal (1,0,0), area 13mm2, adj f15,f16,f17,f69,f70,f126
  f125: plane 5x5mm, normal (-1,0,0), area 13mm2, adj f12,f13,f14,f69,f70,f126
  f126: plane 12.5x1mm, normal (0,0,1), area 12.5mm2, adj f69,f70,f124,f125
  f127: plane 5x5mm, normal (1,0,0), area 13mm2, adj f12,f13,f14,f69,f70,f129
  f128: plane 5x5mm, normal (-1,0,0), area 13mm2, adj f9,f10,f11,f69,f70,f129
  f129: plane 12.5x1mm, normal (0,0,1), area 12.5mm2, adj f69,f70,f127,f128
  f130: plane 5x5mm, normal (1,0,0), area 13mm2, adj f9,f10,f11,f69,f70,f132
  f131: plane 5x5mm, normal (-1,0,0), area 13mm2, adj f6,f7,f8,f69,f70,f132
  f132: plane 12.5x1mm, normal (0,0,1), area 12.5mm2, adj f69,f70,f130,f131
  f133: plane 5x5mm, normal (1,0,0), area 13mm2, adj f6,f7,f8,f69,f70,f135
  f134: plane 5x5mm, normal (-1,0,0), area 13mm2, adj f3,f4,f5,f69,f70,f135
  f135: plane 12.5x1mm, normal (0,0,1), area 12.5mm2, adj f69,f70,f133,f134
  f136: plane 5x5mm, normal (1,0,0), area 13mm2, adj f3,f4,f5,f69,f70,f138
  f137: plane 5x5mm, normal (-1,0,0), area 13mm2, adj f0,f1,f2,f69,f70,f138
  f138: plane 12.5x1mm, normal (0,0,1), area 12.5mm2, adj f69,f70,f136,f137
  f139: plane 5x5mm, normal (1,0,0), area 13mm2, adj f0,f1,f2,f69,f70,f141
  f140: plane 5x5mm, normal (-1,0,0), area 13mm2, adj f69,f70,f71,f74,f75,f141
  f141: plane 12.5x1mm, normal (0,0,1), area 12.5mm2, adj f69,f70,f139,f140
  f142: cylinder r=2mm len=4mm, axis (0,-1,0), area 12.6mm2, adj f69,f70
  f143: cylinder r=2mm len=4mm, axis (0,-1,0), area 12.6mm2, adj f69,f70
  f144: cylinder r=2mm len=4mm, axis (0,-1,0), area 12.6mm2, adj f69,f70
  f145: cylinder r=2mm len=4mm, axis (0,-1,0), area 12.6mm2, adj f69,f70
  f146: cylinder r=2mm len=4mm, axis (0,-1,0), area 12.6mm2, adj f69,f70
  f147: cylinder r=2mm len=4mm, axis (0,-1,0), area 12.6mm2, adj f69,f70
  f148: cylinder r=2mm len=4mm, axis (0,-1,0), area 12.6mm2, adj f69,f70
  f149: cylinder r=2mm len=4mm, axis (0,-1,0), area 12.6mm2, adj f69,f70
  f150: cylinder r=2mm len=4mm, axis (0,-1,0), area 12.6mm2, adj f69,f70
  f151: cylinder r=2mm len=4mm, axis (0,-1,0), area 12.6mm2, adj f69,f70
  f152: cylinder r=2mm len=4mm, axis (0,-1,0), area 12.6mm2, adj f69,f70
PLACE A rot(axis=(0.48,-0.48,0.73),107.7deg) t=(-1.97,-3.29,22.17)mm
PLACE B rot(axis=(-1,0,0),34.2deg) t=(-1.97,-8.81,9.6)mm fixed
PLACE C rot(axis=(-1,0,0),123deg) t=(-1.97,-13.38,30.51)mm
MATE revolute A.f0 <-> C.f1  axis (-1,0,0) through (-1.97,-3.29,22.17)mm
